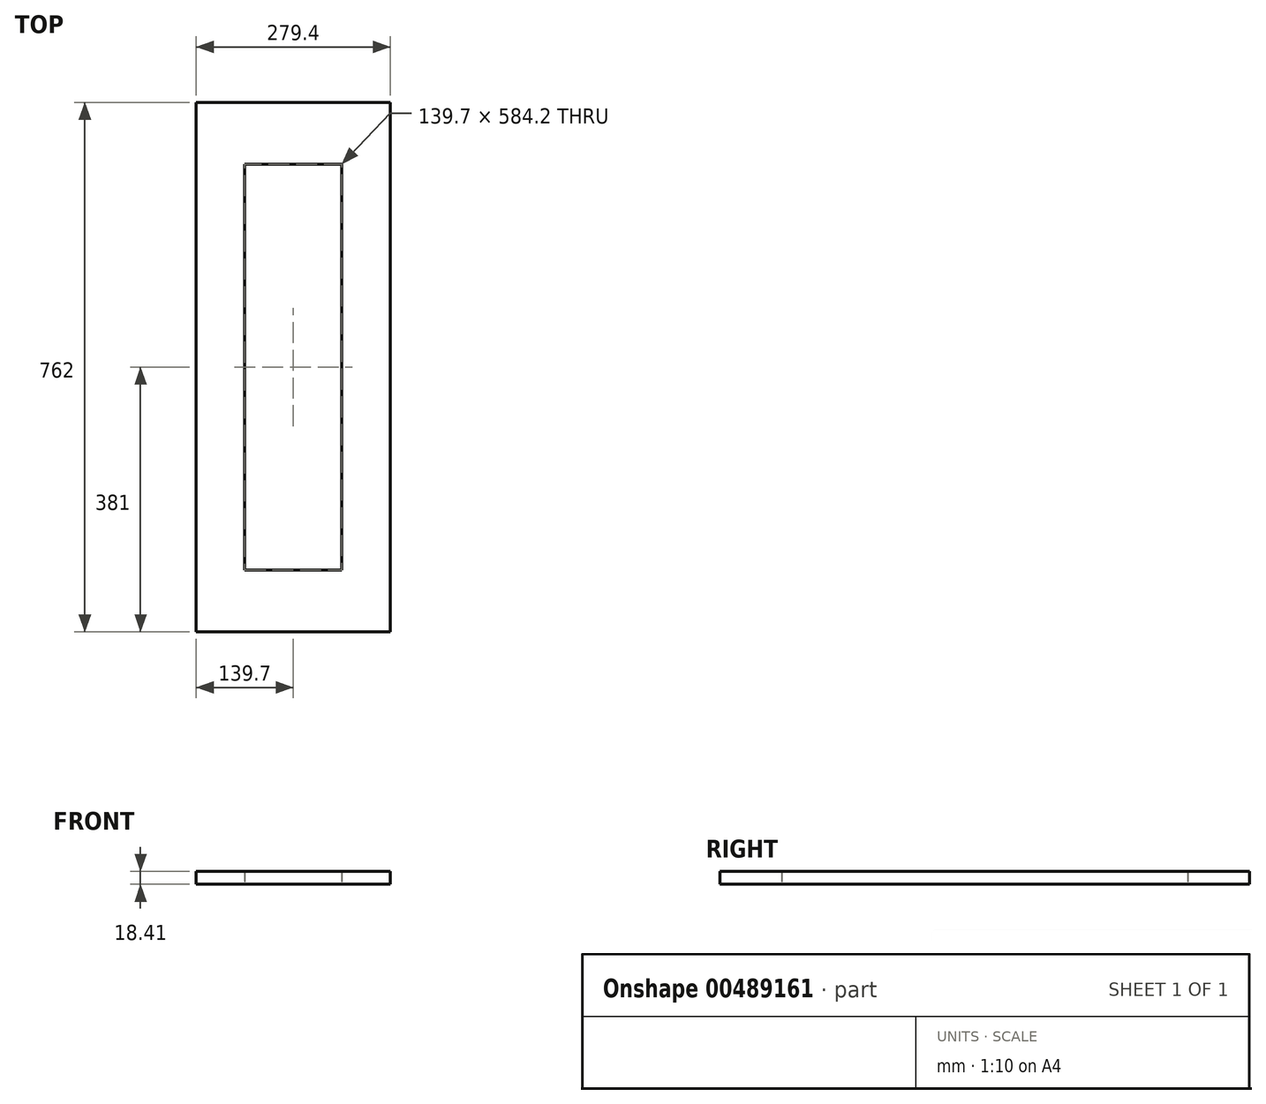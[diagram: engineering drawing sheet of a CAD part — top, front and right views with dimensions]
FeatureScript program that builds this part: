
annotation { "Feature Type Name" : "Feature", "Feature Type Description" : "" }
export const myFeature = defineFeature(function(context is Context, id is Id, definition is map)
    precondition{}
    {
        {
            var Q0;
            Q0=qCreatedBy(makeId("Top.planeOp"),FACE);
            var sketch = newSketch(context, id + "F0", { "sketchPlane" : qUnion([Q0])});
            skLineSegment(sketch, "E0.bottom", {"start": v(0, 0) * mm, "end": v(279.4, 0) * mm});
            skLineSegment(sketch, "E0.top", {"start": v(0, 762) * mm, "end": v(279.4, 762) * mm});
            skLineSegment(sketch, "E0.left", {"start": v(0, 0) * mm, "end": v(0, 762) * mm});
            skLineSegment(sketch, "E0.right", {"start": v(279.4, 0) * mm, "end": v(279.4, 762) * mm});
            skLineSegment(sketch, "E1.bottom", {"start": v(69.85, 673.1) * mm, "end": v(209.55, 673.1) * mm});
            skLineSegment(sketch, "E1.top", {"start": v(69.85, 88.9) * mm, "end": v(209.55, 88.9) * mm});
            skLineSegment(sketch, "E1.left", {"start": v(69.85, 673.1) * mm, "end": v(69.85, 88.9) * mm});
            skLineSegment(sketch, "E1.right", {"start": v(209.55, 673.1) * mm, "end": v(209.55, 88.9) * mm});
            skSolve(sketch);
        }
        {
            var Q0;
            Q0=makeQuery(id+"F0.imprint","IMPRINT",FACE,{"disambiguationData":[TD([[makeQuery(id+"F0.imprint","IMPRINT",EDGE,{"derivedFrom":sQuery(id+"F0.wireOp",EDGE,"E0.bottom")}),1.0]])]});
            extrude(context, id + "F1", {"entities" : qUnion([Q0]), "depth" : 18.41 * mm, "offsetDistance" : 25.4 * mm});
        }
    });
